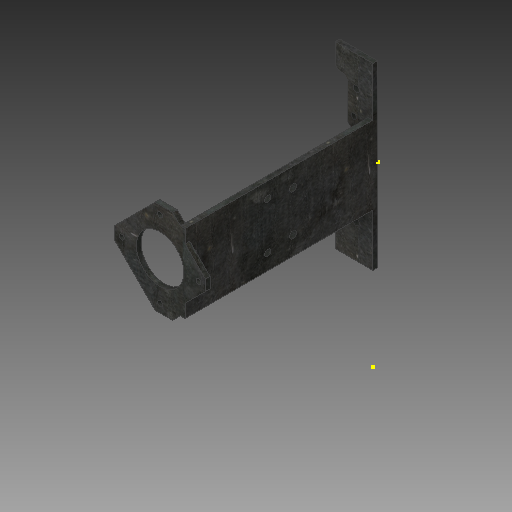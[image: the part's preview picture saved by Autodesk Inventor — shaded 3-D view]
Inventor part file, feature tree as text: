
AUTODESK INVENTOR PART (.ipt)
format: ipt  version: 2018 (Build 220112000, 112)  size: 348,672 bytes
history: native  units: mm
features: sketch x12, reference x12, extrude x9, other x4, plane x2, fillet x1, chamfer x1
ambient origin geometry x8: Origin, YZ Plane, XZ Plane, XY Plane, X Axis, Y Axis, Z Axis, Center Point
bodies: Solid1 (feature_tree)
feature tree (41):
  extrude  "Extrusion1"  Depth=13.0mm
  fillet  "Fillet1"  Radius=30.0mm
  extrude  "Extrusion2"  Depth=55.0mm
  extrude  "Extrusion3"  Depth=16.0mm
  extrude  "Extrusion4"  Depth=7.0mm
  extrude  "Extrusion5"  Depth=6.0mm
  chamfer  "Chamfer1"  Distance=241.0mm
  extrude  "Extrusion6"  Depth=85.0mm TaperAngle=0.0deg
  plane  "Work Plane1"
  plane  "Work Plane2"
  sketch  "Sketch8"  dims[d17=10.0mm d18=10.0mm]
  sketch  "Sketch11"  dims[d19=4.0mm d20=4.0mm]
  sketch  "Sketch13"  dims[d23=7.0mm d24=0.0mm d25=6.0mm]
  sketch  "Sketch15"  dims[d26=40.0mm]
  extrude  "Extrusion19"  Depth=10.0mm
  extrude  "Extrusion20"  Depth=4.0mm
  extrude  "Extrusion21"  Depth=6.0mm
  sketch  "Sketch1"  dims[d0=230.0mm d1=13.0mm d2=30.0mm]
  reference  "Reference1"
  sketch  "Sketch2"  dims[d3=55.0mm d4=55.0mm]
  reference  "Reference2"
  reference  "Reference3"
  sketch  "Sketch3"  dims[d5=55.0mm d6=16.0mm]
  sketch  "Sketch4"  dims[d7=6.0mm d8=0.0mm d9=7.0mm]
  reference  "Reference4"
  reference  "Reference5"
  reference  "Reference6"
  reference  "Reference7"
  sketch  "Sketch5"  dims[d10=100.0mm d11=6.0mm d12=241.0mm d13=0.0mm]
  sketch  "Sketch6"  dims[d14=6.0mm d15=85.0mm d16=0.0mm]
  reference  "Reference8"
  reference  "Reference9"
  reference  "Reference10"
  reference  "Reference11"
  reference  "Reference12"
  sketch  "Sketch23"  dims[d27=26.0mm d28=0.0mm]
  sketch  "Sketch24"  dims[d29=13.0mm d30=2.0mm d31=45.0deg d33=0.5mm d34=7.0mm d35=0.0mm d38=-10.0mm d56=42.0mm d57=24.5mm d58=7.0mm d59=74.0mm d60=21.5mm d61=8.0mm d62=42.0mm d63=74.0mm d64=7.0mm d65=8.0mm d85=16.0mm d86=0.0mm d87=9.0mm d88=24.0mm d89=102.38mm d90=9.0mm d91=102.38mm d92=24.0mm d93=10.0mm d94=0.0mm d95=8.0mm d96=8.0mm d97=20.0mm d98=20.0mm d99=135.0mm d100=10.0mm d101=0.0mm]
  other  "Lathe Model 2018.iam"
  other  "saddle:1"
  other  "Servo Motor:2"
  other  "Body:1"
